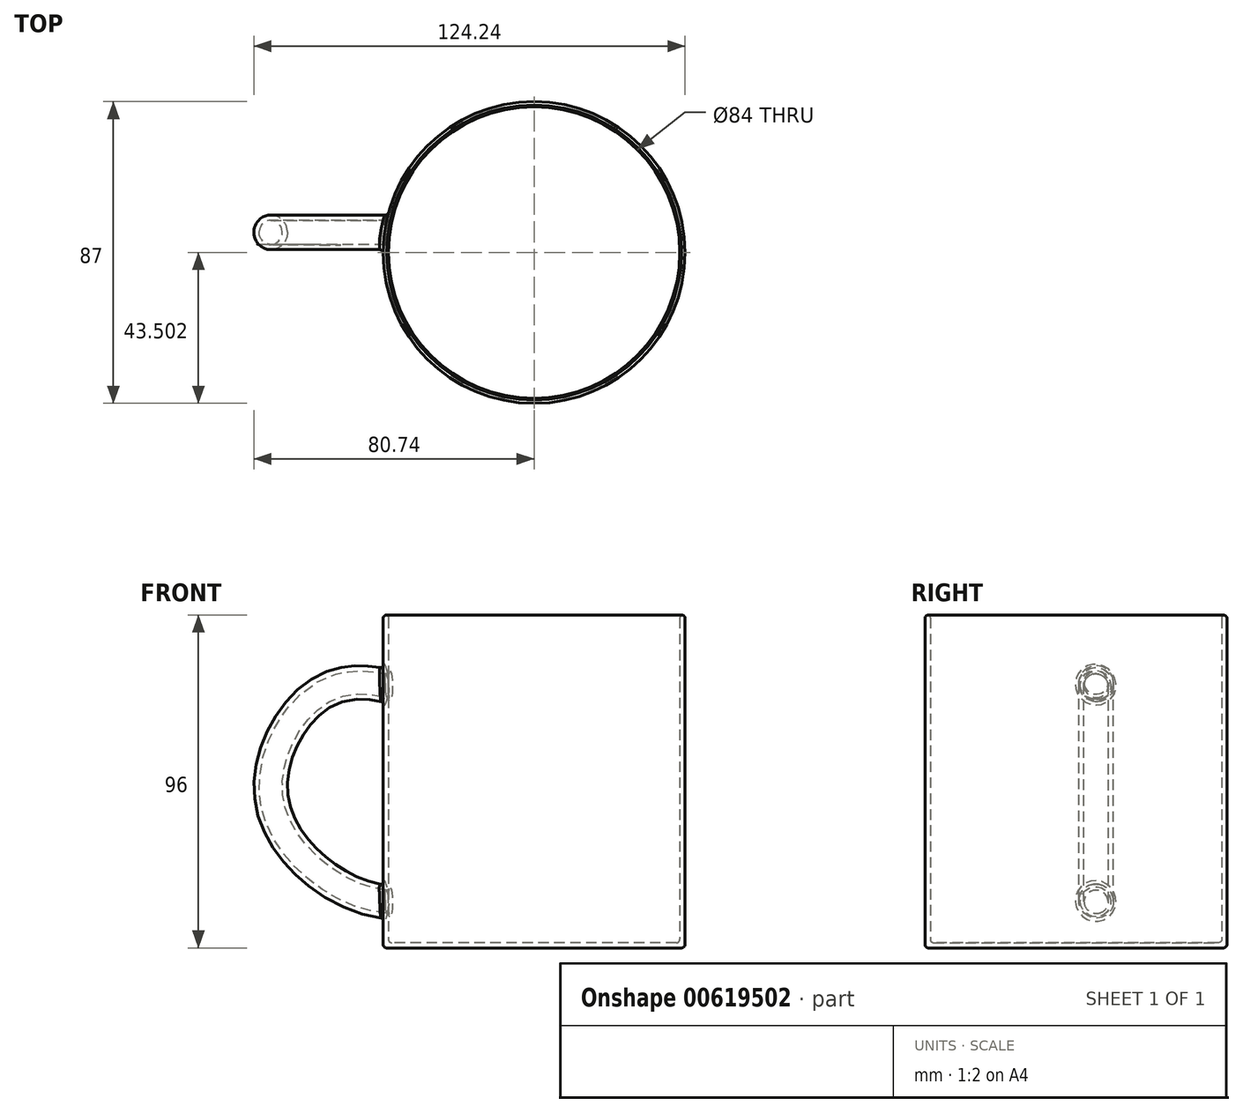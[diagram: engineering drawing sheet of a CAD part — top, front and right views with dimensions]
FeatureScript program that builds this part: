
annotation { "Feature Type Name" : "Feature", "Feature Type Description" : "" }
export const myFeature = defineFeature(function(context is Context, id is Id, definition is map)
    precondition{}
    {
        {
            var Q0;
            Q0=qCreatedBy(makeId("Top.planeOp"),FACE);
            var sketch = newSketch(context, id + "F0", { "sketchPlane" : qUnion([Q0])});
            skCircle(sketch, "E0", {"center": v(0, -5.8) * mm, "radius": 43.5 * mm});
            skSolve(sketch);
        }
        {
            var Q0;
            Q0 = qSketchRegion(id + "F0", true);
            extrude(context, id + "F1", {"entities" : qUnion([Q0]), "depth" : 96 * mm, "offsetDistance" : 25 * mm});
        }
        {
            var Q0;
            Q0=qCreatedBy(makeId("Front.planeOp"),FACE);
            var sketch = newSketch(context, id + "F2", { "sketchPlane" : qUnion([Q0])});
            skFitSpline(sketch, "E1", {"points": [v(-33.28, 70.55) * mm, v(-59.01, 72.03) * mm, v(-73.2, 43.04) * mm, v(-50.14, 17.6) * mm, v(-27.66, 16.42) * mm], "startDerivative": vector(-113.3, 34.92) * mm, "endDerivative": vector(97.28, 12.75) * mm});
            skSolve(sketch);
        }
        {
            var Q0;
            Q0=qCreatedBy(makeId("Right.planeOp"),FACE);
            cPlane(context, id + "F3", {"entities" : qUnion([Q0]), "cplaneType" : CPlaneType.OFFSET, "offset" : 36.7 * mm, "oppositeDirection" : true, "width" : 150 * mm, "height" : 150 * mm});
        }
        {
            var Q0;
            Q0=qCreatedBy(id+"F3.planeOp",FACE);
            var sketch = newSketch(context, id + "F4", { "sketchPlane" : qUnion([Q0])});
            skCircle(sketch, "E2", {"center": v(0, 74.1) * mm, "radius": 5 * mm});
            skSolve(sketch);
        }
        {
            var Q0;
            Q0 = qSketchRegion(id + "F4", true);
            var Q1;
            Q1 = qConstructionFilter(qBodyType(qCreatedBy(id + "F2" ,EDGE), BodyType.WIRE), ConstructionObject.NO);
            sweep(context, id + "F5", {"operationType" : NewBodyOperationType.ADD, "profiles" : qUnion([Q0]), "path" : qUnion([Q1])});
        }
        {
            var Q0;
            Q0=makeQuery(id+"F1.opExtrude","CAP_FACE",FACE,{"disambiguationData":[OSD([sQuery(id+"F0.wireOp",EDGE,"E0")])],"isStart":false});
            shell(context, id + "F6", {"entities" : qUnion([Q0]), "thickness" : 1.5 * mm});
        }
        {
            var Q0;
            {var subQ0=sQuery(id+"F0.wireOp",EDGE,"E0");Q0=makeQuery(id+"F6.opShell","OFFSET_FACE",FACE,{"disambiguationData":[OSD([subQ0]),TDD([makeQuery(id+"F1.opExtrude","CAP_FACE",FACE,{"disambiguationData":[OSD([subQ0])],"isStart":true})])]});}
            fillet(context, id + "F7", {"entities" : qUnion([Q0]), "radius" : 1 * mm, "tangentPropagation" : true, "allowEdgeOverflow" : false});
        }
        {
            var Q0;
            Q0=makeQuery(id+"F1.opExtrude","SWEPT_FACE",FACE,{"disambiguationData":[OSD([sQuery(id+"F0.wireOp",EDGE,"E0")])]});
            fillet(context, id + "F8", {"entities" : qUnion([Q0]), "radius" : 1 * mm, "tangentPropagation" : true, "allowEdgeOverflow" : false});
        }
        {
            var Q0;
            {var subQ0=sQuery(id+"F0.wireOp",EDGE,"E0");Q0=makeQuery(id+"F6.opShell","OFFSET_EDGE",EDGE,{"disambiguationData":[OSD([subQ0]),TDD([makeQuery(id+"F1.opExtrude","CAP_EDGE",EDGE,{"disambiguationData":[OSD([subQ0])],"isStart":false})])]});}
            fillet(context, id + "F9", {"entities" : qUnion([Q0]), "radius" : 1 * mm, "tangentPropagation" : true, "allowEdgeOverflow" : false});
        }
        {
            var Q0;
            {var subQ0=sQuery(id+"F4.wireOp",EDGE,"E2");var subQ1=sQuery(id+"F2.wireOp",EDGE,"E1");var subQ2=sQuery(id+"F0.wireOp",EDGE,"E0");Q0=makeQuery(id+"F6.opShell","OFFSET_EDGE",EDGE,{"disambiguationData":[OSD([subQ2,subQ1,subQ0]),TDD([makeQuery(id+"F5.boolean.opBoolean","INTERSECT",EDGE,{"disambiguationData":[OD(1.0)],"derivedFrom":[makeQuery(id+"F1.opExtrude","SWEPT_FACE",FACE,{"disambiguationData":[OSD([subQ2])]}),makeQuery(id+"F5.opSweep","SWEPT_FACE",FACE,{"disambiguationData":[OSD([subQ1,subQ0])]})]})])]});}
            fillet(context, id + "F10", {"entities" : qUnion([Q0]), "radius" : 1 * mm, "tangentPropagation" : true, "allowEdgeOverflow" : false});
        }
        {
            var Q0;
            {var subQ0=sQuery(id+"F4.wireOp",EDGE,"E2");var subQ1=sQuery(id+"F2.wireOp",EDGE,"E1");var subQ2=sQuery(id+"F0.wireOp",EDGE,"E0");Q0=makeQuery(id+"F6.opShell","OFFSET_EDGE",EDGE,{"disambiguationData":[OSD([subQ2,subQ1,subQ0]),TDD([makeQuery(id+"F5.boolean.opBoolean","INTERSECT",EDGE,{"disambiguationData":[OD(0.0)],"derivedFrom":[makeQuery(id+"F1.opExtrude","SWEPT_FACE",FACE,{"disambiguationData":[OSD([subQ2])]}),makeQuery(id+"F5.opSweep","SWEPT_FACE",FACE,{"disambiguationData":[OSD([subQ1,subQ0])]})]})])]});}
            fillet(context, id + "F11", {"entities" : qUnion([Q0]), "radius" : 1 * mm, "tangentPropagation" : true, "allowEdgeOverflow" : false});
        }
    });
